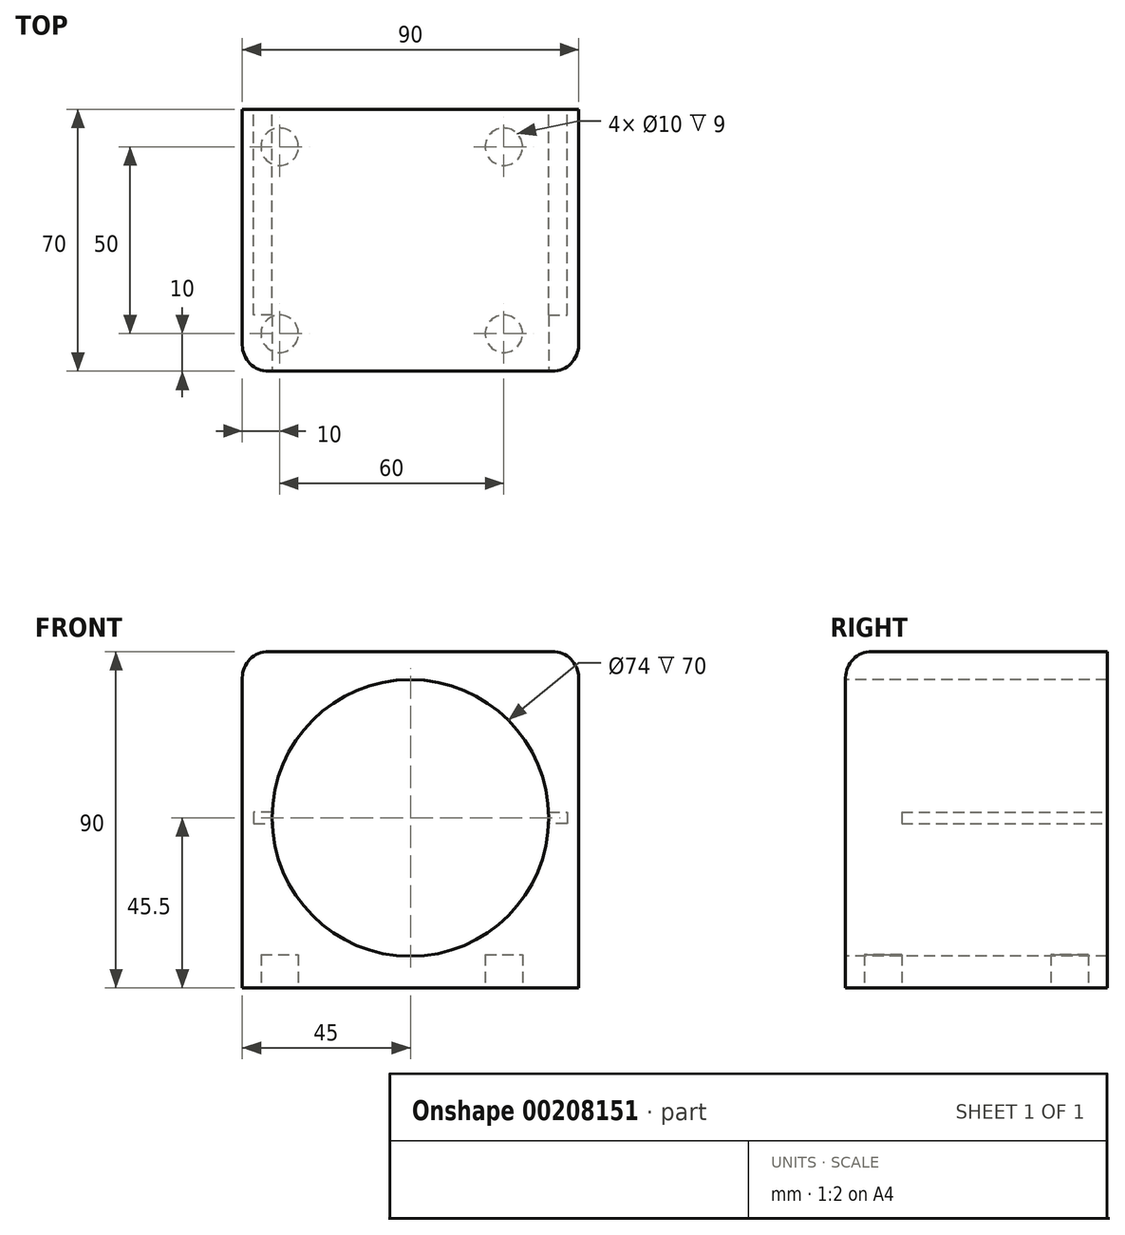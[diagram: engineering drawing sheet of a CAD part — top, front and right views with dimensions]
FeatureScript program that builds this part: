
annotation { "Feature Type Name" : "Feature", "Feature Type Description" : "" }
export const myFeature = defineFeature(function(context is Context, id is Id, definition is map)
    precondition{}
    {
        {
            var Q0;
            Q0=qCreatedBy(makeId("Top.planeOp"),FACE);
            var sketch = newSketch(context, id + "F0", { "sketchPlane" : qUnion([Q0])});
            skLineSegment(sketch, "E0.bottom", {"start": v(45, 35) * mm, "end": v(-45, 35) * mm});
            skLineSegment(sketch, "E0.top", {"start": v(45, -35) * mm, "end": v(-45, -35) * mm});
            skLineSegment(sketch, "E0.left", {"start": v(45, 35) * mm, "end": v(45, -35) * mm});
            skLineSegment(sketch, "E0.right", {"start": v(-45, 35) * mm, "end": v(-45, -35) * mm});
            skPoint(sketch, "E0.middle", {"position": v(0, 0) * mm});
            skSolve(sketch);
        }
        {
            var Q0;
            Q0=makeQuery(id+"F0.imprint","IMPRINT",FACE,{"disambiguationData":[TD([[makeQuery(id+"F0.imprint","IMPRINT",EDGE,{"derivedFrom":sQuery(id+"F0.wireOp",EDGE,"E0.bottom")}),1.0]])]});
            extrude(context, id + "F1", {"entities" : qUnion([Q0]), "depth" : 90 * mm});
        }
        {
            var Q0;
            Q0=makeQuery(id+"F1.opExtrude","SWEPT_FACE",FACE,{"disambiguationData":[OSD([sQuery(id+"F0.wireOp",EDGE,"E0.top")])]});
            var sketch = newSketch(context, id + "F2", { "sketchPlane" : qUnion([Q0])});
            skCircle(sketch, "E1", {"center": v(0, 45.5) * mm, "radius": 37 * mm});
            skSolve(sketch);
        }
        {
            var Q0;
            Q0=makeQuery(id+"F2.imprint","IMPRINT",FACE,{"disambiguationData":[TD([[makeQuery(id+"F2.imprint","IMPRINT",EDGE,{"derivedFrom":sQuery(id+"F2.wireOp",EDGE,"E1")}),1.0]])]});
            extrude(context, id + "F3", {"entities" : qUnion([Q0]), "operationType" : NewBodyOperationType.REMOVE, "oppositeDirection" : true, "depth" : 70 * mm});
        }
        {
            var Q0;
            Q0=makeQuery(id+"F1.opExtrude","CAP_FACE",FACE,{"disambiguationData":[OSD([sQuery(id+"F0.wireOp",EDGE,"E0.bottom"),sQuery(id+"F0.wireOp",EDGE,"E0.top"),sQuery(id+"F0.wireOp",EDGE,"E0.left"),sQuery(id+"F0.wireOp",EDGE,"E0.right")])],"isStart":true});
            var sketch = newSketch(context, id + "F4", { "sketchPlane" : qUnion([Q0])});
            skCircle(sketch, "E2", {"center": v(-35, -25) * mm, "radius": 5 * mm});
            skCircle(sketch, "E3.0.1.0", {"center": v(-35, 25) * mm, "radius": 5 * mm});
            skCircle(sketch, "E3.1.0.0", {"center": v(25, -25) * mm, "radius": 5 * mm});
            skCircle(sketch, "E3.1.1.0", {"center": v(25, 25) * mm, "radius": 5 * mm});
            skLineSegment(sketch, "E3.direction1", {"start": v(-35, -25) * mm, "end": v(25, -25) * mm, "construction": true});
            skLineSegment(sketch, "E3.direction2", {"start": v(-35, -25) * mm, "end": v(-35, 25) * mm, "construction": true});
            skSolve(sketch);
        }
        {
            var Q0;
            Q0=makeQuery(id+"F4.imprint","IMPRINT",FACE,{"disambiguationData":[TD([[makeQuery(id+"F4.imprint","IMPRINT",EDGE,{"derivedFrom":sQuery(id+"F4.wireOp",EDGE,"E3.0.1.0")}),1.0]])]});
            var Q1;
            Q1=makeQuery(id+"F4.imprint","IMPRINT",FACE,{"disambiguationData":[TD([[makeQuery(id+"F4.imprint","IMPRINT",EDGE,{"derivedFrom":sQuery(id+"F4.wireOp",EDGE,"E2")}),1.0]])]});
            var Q2;
            Q2=makeQuery(id+"F4.imprint","IMPRINT",FACE,{"disambiguationData":[TD([[makeQuery(id+"F4.imprint","IMPRINT",EDGE,{"derivedFrom":sQuery(id+"F4.wireOp",EDGE,"E3.1.1.0")}),1.0]])]});
            var Q3;
            Q3=makeQuery(id+"F4.imprint","IMPRINT",FACE,{"disambiguationData":[TD([[makeQuery(id+"F4.imprint","IMPRINT",EDGE,{"derivedFrom":sQuery(id+"F4.wireOp",EDGE,"E3.1.0.0")}),1.0]])]});
            var Q4;
            Q4=sQuery(id+"F4.wireOp",EDGE,"E3.0.1.0");
            var Q5;
            Q5=sQuery(id+"F4.wireOp",EDGE,"E2");
            var Q6;
            Q6=sQuery(id+"F4.wireOp",EDGE,"E3.1.1.0");
            var Q7;
            Q7=sQuery(id+"F4.wireOp",EDGE,"E3.1.0.0");
            extrude(context, id + "F5", {"entities" : qUnion([Q0, Q1, Q2, Q3]), "operationType" : NewBodyOperationType.REMOVE, "surfaceEntities" : qUnion([Q4, Q5, Q6, Q7]), "oppositeDirection" : true, "depth" : 9 * mm});
        }
        {
            var Q0;
            Q0=makeQuery(id+"F1.opExtrude","CAP_EDGE",EDGE,{"disambiguationData":[OSD([sQuery(id+"F0.wireOp",EDGE,"E0.top")])],"isStart":false});
            var Q1;
            Q1=makeQuery(id+"F1.opExtrude","CAP_EDGE",EDGE,{"disambiguationData":[OSD([sQuery(id+"F0.wireOp",EDGE,"E0.left")])],"isStart":false});
            var Q2;
            Q2=makeQuery(id+"F1.opExtrude","CAP_EDGE",EDGE,{"disambiguationData":[OSD([sQuery(id+"F0.wireOp",EDGE,"E0.right")])],"isStart":false});
            var Q3;
            Q3=makeQuery(id+"F1.opExtrude","SWEPT_EDGE",EDGE,{"disambiguationData":[OSD([sQuery(id+"F0.wireOp",EDGE,"E0.top"),sQuery(id+"F0.wireOp",EDGE,"E0.left")])]});
            var Q4;
            Q4=makeQuery(id+"F1.opExtrude","SWEPT_EDGE",EDGE,{"disambiguationData":[OSD([sQuery(id+"F0.wireOp",EDGE,"E0.top"),sQuery(id+"F0.wireOp",EDGE,"E0.right")])]});
            fillet(context, id + "F6", {"entities" : qUnion([Q0, Q1, Q2, Q3, Q4]), "radius" : 7 * mm, "tangentPropagation" : true, "allowEdgeOverflow" : false});
        }
        {
            var Q0;
            Q0=makeQuery(id+"F1.opExtrude","SWEPT_FACE",FACE,{"disambiguationData":[OSD([sQuery(id+"F0.wireOp",EDGE,"E0.bottom")])]});
            var sketch = newSketch(context, id + "F7", { "sketchPlane" : qUnion([Q0])});
            skLineSegment(sketch, "E4", {"start": v(36.97, 47) * mm, "end": v(41.97, 47) * mm});
            skLineSegment(sketch, "E5", {"start": v(41.97, 47) * mm, "end": v(41.97, 45.5) * mm});
            skLineSegment(sketch, "E6", {"start": v(41.97, 45.5) * mm, "end": v(41.97, 44) * mm});
            skLineSegment(sketch, "E7", {"start": v(41.97, 44) * mm, "end": v(36.97, 44) * mm});
            skLineSegment(sketch, "E8", {"start": v(-36.97, 47) * mm, "end": v(-41.97, 47) * mm});
            skLineSegment(sketch, "E9", {"start": v(-41.97, 47) * mm, "end": v(-41.97, 45.5) * mm});
            skLineSegment(sketch, "E10", {"start": v(-41.97, 45.5) * mm, "end": v(-41.97, 44) * mm});
            skLineSegment(sketch, "E11", {"start": v(-41.97, 44) * mm, "end": v(-36.97, 44) * mm});
            skSolve(sketch);
        }
        {
            var Q0;
            {var subQ1=sQuery(id+"F7.wireOp",EDGE,"E8");Q0=makeQuery(id+"F7.imprint","IMPRINT",FACE,{"disambiguationData":[TD([[makeQuery(id+"F7.imprint","IMPRINT",EDGE,{"derivedFrom":subQ1}),1.0]])]});}
            var Q1;
            {var subQ1=sQuery(id+"F7.wireOp",EDGE,"E4");Q1=makeQuery(id+"F7.imprint","IMPRINT",FACE,{"disambiguationData":[TD([[makeQuery(id+"F7.imprint","IMPRINT",EDGE,{"derivedFrom":subQ1}),-1.0]])]});}
            extrude(context, id + "F8", {"entities" : qUnion([Q0, Q1]), "operationType" : NewBodyOperationType.REMOVE, "oppositeDirection" : true, "depth" : 55 * mm});
        }
    });
